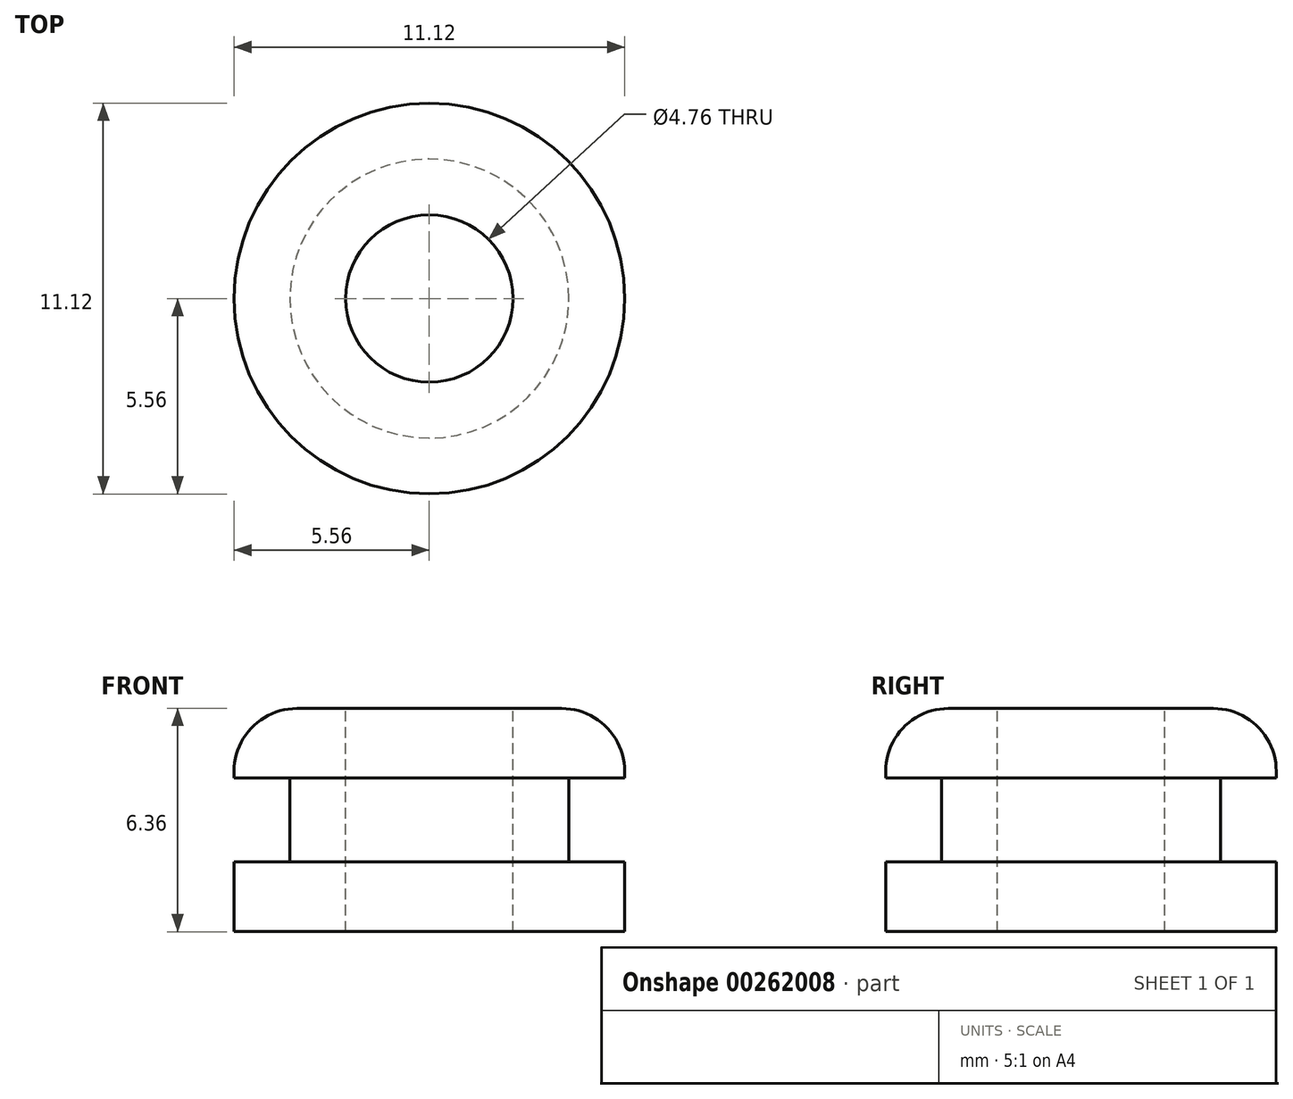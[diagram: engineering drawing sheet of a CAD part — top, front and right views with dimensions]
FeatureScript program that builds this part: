
annotation { "Feature Type Name" : "Feature", "Feature Type Description" : "" }
export const myFeature = defineFeature(function(context is Context, id is Id, definition is map)
    precondition{}
    {
        {
            assignVariable(context, id + "F0", {"name" : "A_ID", "anyValue" : 4.76});
        }
        {
            assignVariable(context, id + "F1", {"name" : "A_r", "anyValue" : getVariable(context, 'A_ID') / 2 * mm});
        }
        {
            var Q0;
            Q0=qCreatedBy(makeId("Front.planeOp"),FACE);
            var sketch = newSketch(context, id + "F2", { "sketchPlane" : qUnion([Q0])});
            skLineSegment(sketch, "E0", {"start": v(0, 12.22) * mm, "end": v(0, -12.17) * mm, "construction": true});
            skLineSegment(sketch, "E1", {"start": v(-2.38, 3.18) * mm, "end": v(-2.38, -3.18) * mm});
            skLineSegment(sketch, "E2", {"start": v(-2.38, -3.18) * mm, "end": v(-5.56, -3.18) * mm});
            skLineSegment(sketch, "E3", {"start": v(-5.56, -3.17) * mm, "end": v(-5.56, -1.2) * mm});
            skLineSegment(sketch, "E4", {"start": v(-5.56, -1.2) * mm, "end": v(-3.97, -1.2) * mm});
            skLineSegment(sketch, "E5", {"start": v(-3.97, -1.2) * mm, "end": v(-3.97, 1.2) * mm});
            skLineSegment(sketch, "E6", {"start": v(-3.97, 1.2) * mm, "end": v(-5.56, 1.2) * mm});
            skLineSegment(sketch, "E7", {"start": v(-5.56, 1.2) * mm, "end": v(-5.56, 3.17) * mm});
            skLineSegment(sketch, "E8", {"start": v(-5.56, 3.17) * mm, "end": v(-2.38, 3.17) * mm});
            skPoint(sketch, "E9", {"position": v(-2.38, 0) * mm});
            skPoint(sketch, "E9.positionSnap0", {"position": v(-2.38, 0) * mm});
            skPoint(sketch, "E10", {"position": v(-3.97, 0) * mm});
            skSolve(sketch);
        }
        {
            var Q0;
            Q0=makeQuery(id+"F2.imprint","IMPRINT",FACE,{"disambiguationData":[TD([[makeQuery(id+"F2.imprint","IMPRINT",EDGE,{"derivedFrom":sQuery(id+"F2.wireOp",EDGE,"E1")}),-1.0]])]});
            var Q1;
            Q1=sQuery(id+"F2.wireOp",EDGE,"E0");
            revolve(context, id + "F3", {"entities" : qUnion([Q0]), "axis" : qUnion([Q1]), "revolveType" : RevolveType.FULL});
        }
        {
            var Q0;
            Q0=makeQuery(id+"F3.opRevolve","SWEPT_EDGE",EDGE,{"disambiguationData":[OSD([sQuery(id+"F2.wireOp",EDGE,"E7"),sQuery(id+"F2.wireOp",EDGE,"E8")])]});
            fillet(context, id + "F4", {"entities" : qUnion([Q0]), "radius" : getVariable(context, 'A_r') * .75, "tangentPropagation" : true, "allowEdgeOverflow" : false});
        }
    });
